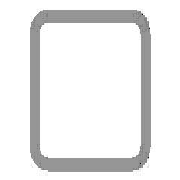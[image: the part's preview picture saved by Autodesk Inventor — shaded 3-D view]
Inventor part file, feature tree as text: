
AUTODESK INVENTOR PART (.ipt)
format: ipt  version: 2025 (Build 290162010, 162A)  size: 139,264 bytes
history: native  units: mm (DEFAULTED — no unit token found)
features: other x4, plane x3, split x2, sketch x1
ambient origin geometry x8: Origin, YZ Plane, XZ Plane, XY Plane, X Axis, Y Axis, Z Axis, Center Point
bodies: Solid1 (feature_tree), Body (feature_tree)
feature tree (10):
  parser-record x1  (decoder bookkeeping rows leaked as tree rows — omitted from the tree; the rows remain in map.json)
  other  "Driven Length"
  other  "Start Plane"
  other  "End Plane"
  plane  "Work Plane4"
  split  "Split1"
  plane  "Work Plane5"
  split  "Split2"
  sketch  "Sketch3"  dims[d3=1600.0mm d4=0.0mm d7=8.0mm d9=60.0mm d11=60.0mm d12=4.0mm d13=60.0mm d14=1660.0mm d15=30.0mm d16=30.0mm d17=90.0deg d18=1600.0mm]
  plane  "Work Plane3"
